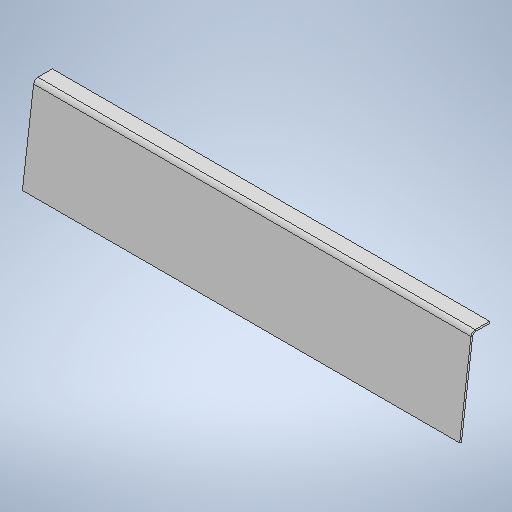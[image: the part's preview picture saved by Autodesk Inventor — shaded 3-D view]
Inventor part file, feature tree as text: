
AUTODESK INVENTOR PART (.ipt)
format: ipt  version: 2025 (Build 290162010, 162A)  size: 283,136 bytes
history: native  units: mm
features: sheet_metal_op x4, other x3, sketch x2
ambient origin geometry x8: Origin, YZ Plane, XZ Plane, XY Plane, X Axis, Y Axis, Z Axis, Center Point
bodies: Body1 (feature_tree)
feature tree (9):
  sheet_metal_op  "Face2"
  sheet_metal_op  "Flange5"
  sketch  "Sketch7"  dims[d52=480.0mm]
  other  "Plate6"
  sketch  "Sketch8"  dims[d53=20.0mm d54=2.0mm d55=2.0mm d56=1.0mm d57=4.0mm d58=2.75mm d59=100.0mm d60=14.416071mm d61=2.75mm d62=8.0mm d63=2.0mm d64=2.75mm]
  other  "Plate7"
  sheet_metal_op  "Bend5"
  sheet_metal_op  "Corner5"
  other  "Definition1"
